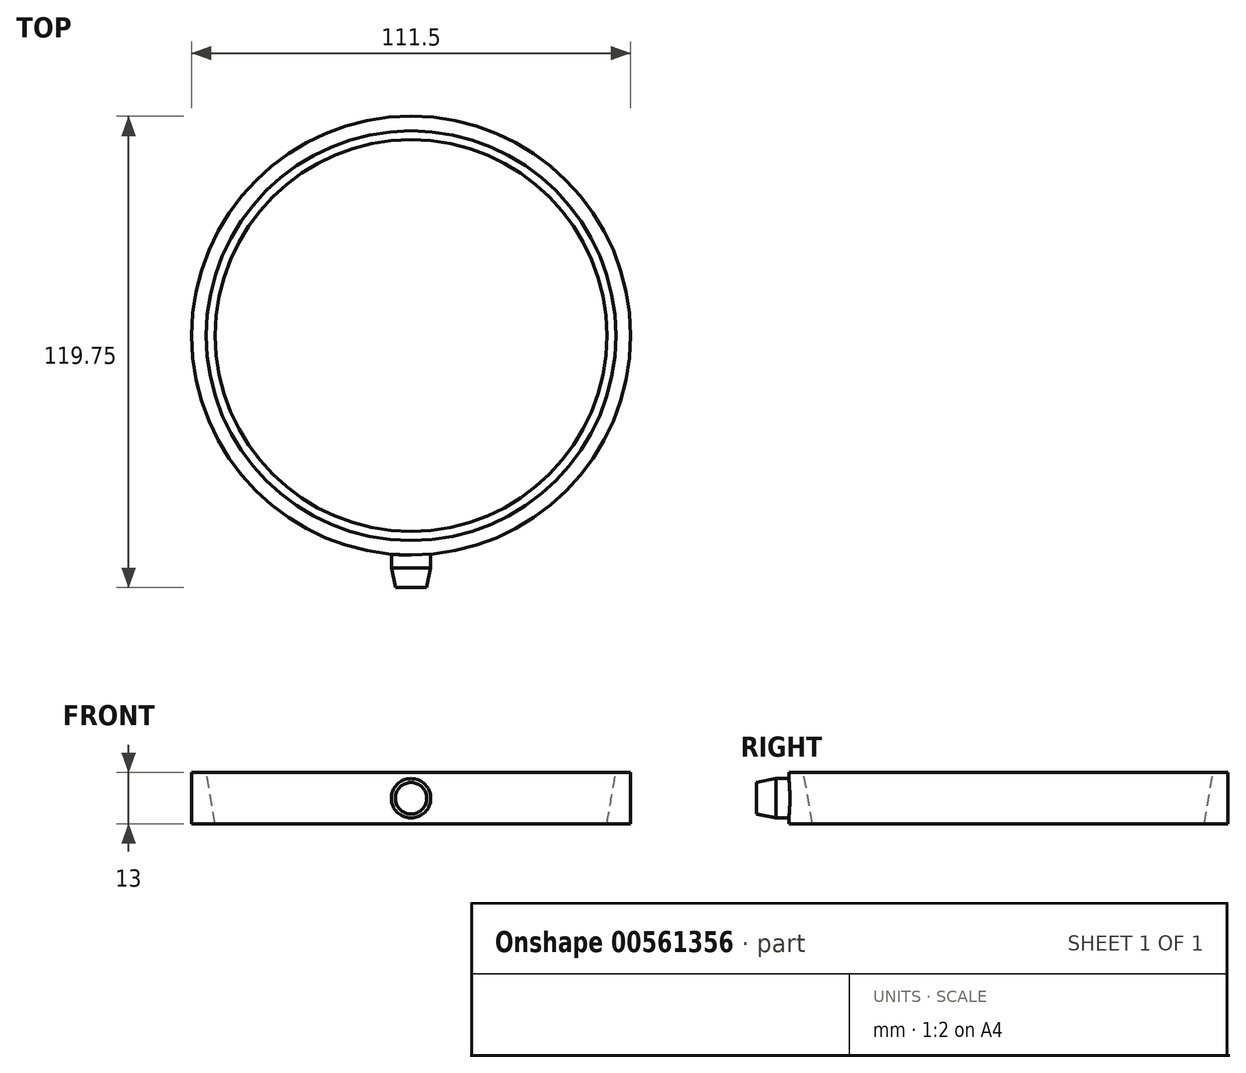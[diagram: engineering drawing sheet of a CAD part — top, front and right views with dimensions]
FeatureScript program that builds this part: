
annotation { "Feature Type Name" : "Feature", "Feature Type Description" : "" }
export const myFeature = defineFeature(function(context is Context, id is Id, definition is map)
    precondition{}
    {
        {
            var Q0;
            Q0=qCreatedBy(makeId("Top.planeOp"),FACE);
            var sketch = newSketch(context, id + "F0", { "sketchPlane" : qUnion([Q0])});
            skCircle(sketch, "E0", {"center": v(0, 0) * mm, "radius": 49.75 * mm});
            skCircle(sketch, "E1.0", {"center": v(0, 0) * mm, "radius": 55.75 * mm});
            skSolve(sketch);
        }
        {
            var Q0;
            Q0=makeQuery(id+"F0.imprint","IMPRINT",FACE,{"disambiguationData":[TD([[makeQuery(id+"F0.imprint","IMPRINT",EDGE,{"derivedFrom":sQuery(id+"F0.wireOp",EDGE,"E0")}),-1.0]])]});
            extrude(context, id + "F1", {"entities" : qUnion([Q0]), "depth" : 13 * mm, "offsetDistance" : 25 * mm});
        }
        {
            var Q0;
            Q0=qCreatedBy(makeId("Front.planeOp"),FACE);
            cPlane(context, id + "F2", {"entities" : qUnion([Q0]), "cplaneType" : CPlaneType.OFFSET, "offset" : 54 * mm, "width" : 150 * mm, "height" : 150 * mm});
        }
        {
            var Q0;
            Q0=qCreatedBy(id+"F2.planeOp",FACE);
            var sketch = newSketch(context, id + "F3", { "sketchPlane" : qUnion([Q0])});
            skCircle(sketch, "E2", {"center": v(0, 6.46) * mm, "radius": 5 * mm});
            skSolve(sketch);
        }
        {
            var Q0;
            Q0 = qSketchRegion(id + "F3", true);
            var Q1;
            Q1=sQuery(id+"F3.wireOp",EDGE,"E2");
            extrude(context, id + "F4", {"entities" : qUnion([Q0]), "operationType" : NewBodyOperationType.ADD, "surfaceEntities" : qUnion([Q1]), "depth" : 10 * mm, "offsetDistance" : 25 * mm});
        }
        {
            var Q0;
            Q0=makeQuery(id+"F1.opExtrude","CAP_EDGE",EDGE,{"disambiguationData":[OSD([sQuery(id+"F0.wireOp",EDGE,"E0")])],"isStart":false});
            chamfer(context, id + "F5", {"entities" : qUnion([Q0]), "chamferType" : ChamferType.OFFSET_ANGLE, "width" : 13 * mm, "oppositeDirection" : false, "angle" : 10 * degree, "tangentPropagation" : true});
        }
        {
            var Q0;
            Q0=makeQuery(id+"F4.opExtrude","CAP_EDGE",EDGE,{"disambiguationData":[OSD([sQuery(id+"F3.wireOp",EDGE,"E2")])],"isStart":false});
            chamfer(context, id + "F6", {"entities" : qUnion([Q0]), "chamferType" : ChamferType.TWO_OFFSETS, "width1" : 1 * mm, "oppositeDirection" : false, "width2" : 5 * mm, "tangentPropagation" : true});
        }
    });
